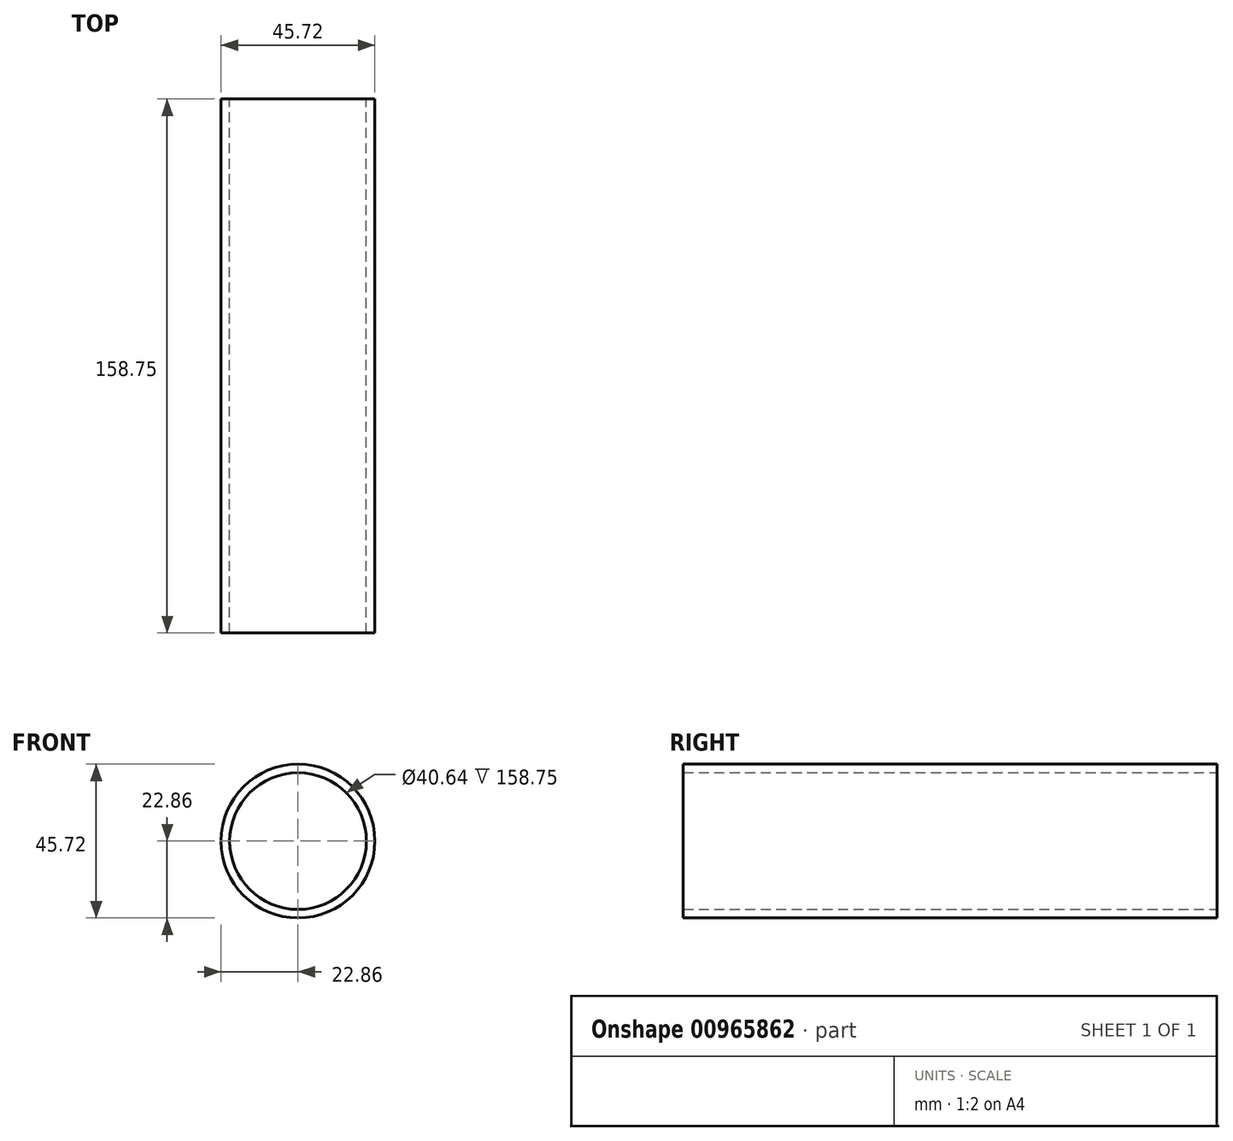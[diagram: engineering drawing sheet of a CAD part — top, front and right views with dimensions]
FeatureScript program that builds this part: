
annotation { "Feature Type Name" : "Feature", "Feature Type Description" : "" }
export const myFeature = defineFeature(function(context is Context, id is Id, definition is map)
    precondition{}
    {
        {
            var Q0;
            Q0=qCreatedBy(makeId("Front.planeOp"),FACE);
            var sketch = newSketch(context, id + "F0", { "sketchPlane" : qUnion([Q0])});
            skCircle(sketch, "E0", {"center": v(0, 0) * mm, "radius": 22.86 * mm});
            skCircle(sketch, "E1", {"center": v(0, 0) * mm, "radius": 20.32 * mm});
            skSolve(sketch);
        }
        {
            var Q0;
            Q0 = qSketchRegion(id + "F0", true);
            extrude(context, id + "F1", {"entities" : qUnion([Q0]), "depth" : 158.75 * mm, "offsetDistance" : 25.4 * mm});
        }
    });
